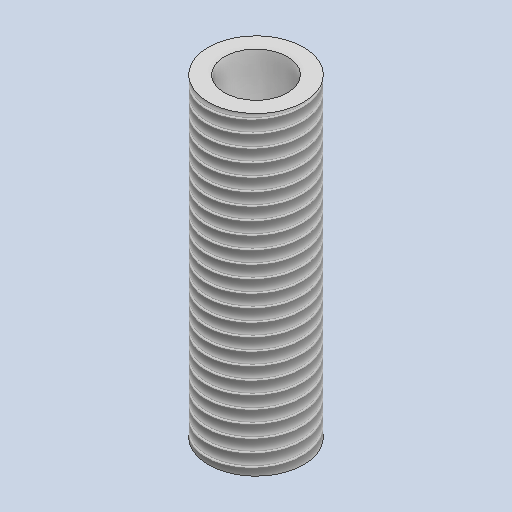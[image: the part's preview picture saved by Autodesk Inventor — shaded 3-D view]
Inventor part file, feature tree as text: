
AUTODESK INVENTOR PART (.ipt)
format: ipt  version: 2024 (Build 280153000, 153)  size: 159,232 bytes
history: native  units: mm
features: other x4, sketch x2
ambient origin geometry x8: Origin, YZ Plane, XZ Plane, XY Plane, X Axis, Y Axis, Z Axis, Center Point
bodies: Body1 (feature_tree)
feature tree (6):
  other  "TORNILLO_B_MIR.ipt"
  other  "Sólido1::TORNILLO_B_MIR.ipt"
  other  "OperaciónIdentificador1"
  sketch  "Boceto1"  dims[d0=10.0mm]
  sketch  "Boceto2"
  other  "Sólido1"
